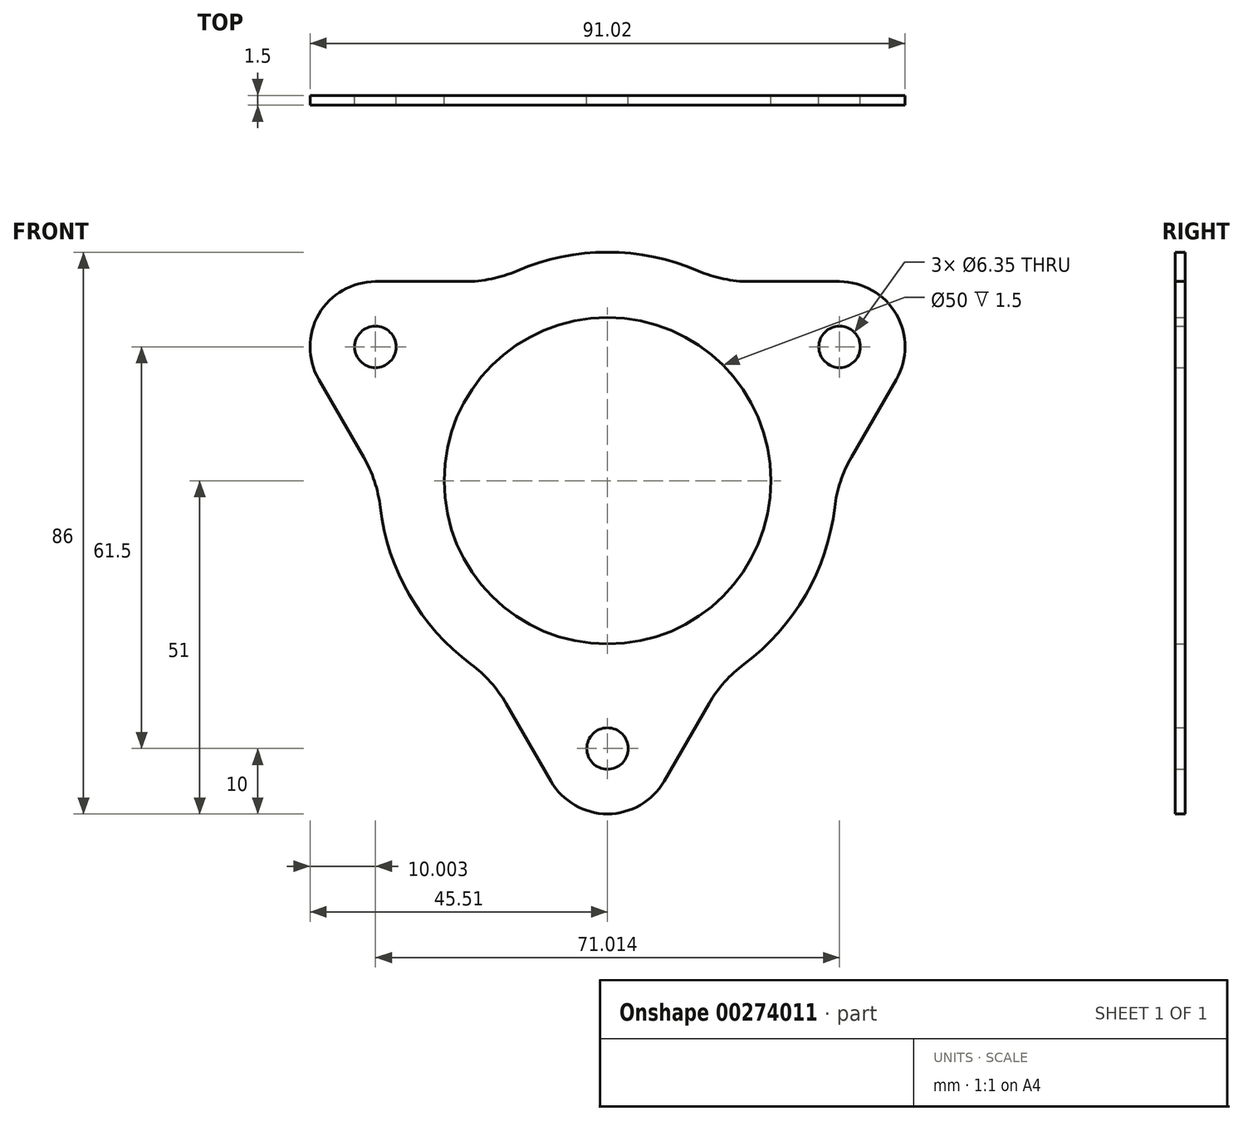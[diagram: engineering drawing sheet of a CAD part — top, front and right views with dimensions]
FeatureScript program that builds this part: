
annotation { "Feature Type Name" : "Feature", "Feature Type Description" : "" }
export const myFeature = defineFeature(function(context is Context, id is Id, definition is map)
    precondition{}
    {
        {
            var Q0;
            Q0=qCreatedBy(makeId("Front.planeOp"),FACE);
            var sketch = newSketch(context, id + "F0", { "sketchPlane" : qUnion([Q0])});
            skCircle(sketch, "E0", {"center": v(0, 0) * mm, "radius": 25 * mm});
            skCircle(sketch, "E1", {"center": v(0, 0) * mm, "radius": 41 * mm, "construction": true});
            skLineSegment(sketch, "E2", {"start": v(0, 0) * mm, "end": v(35.5, 20.5) * mm, "construction": true});
            skLineSegment(sketch, "E3", {"start": v(0, 0) * mm, "end": v(0, -41) * mm, "construction": true});
            skLineSegment(sketch, "E4", {"start": v(0, 0) * mm, "end": v(-35.5, 20.5) * mm, "construction": true});
            skCircle(sketch, "E5", {"center": v(-35.5, 20.5) * mm, "radius": 3.17 * mm});
            skCircle(sketch, "E6", {"center": v(35.5, 20.5) * mm, "radius": 3.17 * mm});
            skCircle(sketch, "E7", {"center": v(0, -41) * mm, "radius": 3.17 * mm});
            skArc(sketch, "E8", {"start": v(-8.66, -46) * mm, "mid": v(0, -51) * mm, "end": v(8.66, -46) * mm});
            skArc(sketch, "E9", {"start": v(-35.5, 30.5) * mm, "mid": v(-44.17, 25.5) * mm, "end": v(-44.17, 15.5) * mm});
            skArc(sketch, "E10", {"start": v(44.17, 15.5) * mm, "mid": v(44.17, 25.5) * mm, "end": v(35.5, 30.5) * mm});
            skLineSegment(sketch, "E11", {"start": v(-35.5, 30.5) * mm, "end": v(-17.17, 30.5) * mm});
            skLineSegment(sketch, "E12", {"start": v(-44.17, 15.5) * mm, "end": v(-35, -0.38) * mm});
            skLineSegment(sketch, "E13", {"start": v(8.66, -46) * mm, "end": v(17.83, -30.12) * mm});
            skArc(sketch, "E14", {"start": v(-35, -0.38) * mm, "mid": v(-30.31, -17.5) * mm, "end": v(-17.83, -30.12) * mm});
            skLineSegment(sketch, "E15.trimOffspring", {"start": v(17.17, 30.5) * mm, "end": v(35.5, 30.5) * mm});
            skLineSegment(sketch, "E16.trimOffspring", {"start": v(-17.83, -30.12) * mm, "end": v(-8.66, -46) * mm});
            skArc(sketch, "E17.trimOffspring", {"start": v(17.83, -30.12) * mm, "mid": v(30.31, -17.5) * mm, "end": v(35, -0.38) * mm});
            skLineSegment(sketch, "E18.trimOffspring", {"start": v(35, -0.38) * mm, "end": v(44.17, 15.5) * mm});
            skArc(sketch, "E19.trimOffspring", {"start": v(17.17, 30.5) * mm, "mid": v(0, 35) * mm, "end": v(-17.17, 30.5) * mm});
            skSolve(sketch);
        }
        {
            var Q0;
            Q0=qSketchRegion(id+"F0",true);
            extrude(context, id + "F1", {"entities" : qUnion([Q0]), "depth" : 1.5 * mm});
        }
        {
            var Q0;
            Q0=makeQuery(id+"F1.opExtrude","SWEPT_EDGE",EDGE,{"disambiguationData":[OSD([sQuery(id+"F0.wireOp",EDGE,"E17.trimOffspring"),sQuery(id+"F0.wireOp",EDGE,"E18.trimOffspring")])]});
            var Q1;
            Q1=makeQuery(id+"F1.opExtrude","SWEPT_EDGE",EDGE,{"disambiguationData":[OSD([sQuery(id+"F0.wireOp",EDGE,"E15.trimOffspring"),sQuery(id+"F0.wireOp",EDGE,"E19.trimOffspring")])]});
            var Q2;
            Q2=makeQuery(id+"F1.opExtrude","SWEPT_EDGE",EDGE,{"disambiguationData":[OSD([sQuery(id+"F0.wireOp",EDGE,"E11"),sQuery(id+"F0.wireOp",EDGE,"E19.trimOffspring")])]});
            var Q3;
            Q3=makeQuery(id+"F1.opExtrude","SWEPT_EDGE",EDGE,{"disambiguationData":[OSD([sQuery(id+"F0.wireOp",EDGE,"E12"),sQuery(id+"F0.wireOp",EDGE,"E14")])]});
            var Q4;
            Q4=makeQuery(id+"F1.opExtrude","SWEPT_EDGE",EDGE,{"disambiguationData":[OSD([sQuery(id+"F0.wireOp",EDGE,"E14"),sQuery(id+"F0.wireOp",EDGE,"E16.trimOffspring")])]});
            var Q5;
            Q5=makeQuery(id+"F1.opExtrude","SWEPT_EDGE",EDGE,{"disambiguationData":[OSD([sQuery(id+"F0.wireOp",EDGE,"E13"),sQuery(id+"F0.wireOp",EDGE,"E17.trimOffspring")])]});
            fillet(context, id + "F2", {"entities" : qUnion([Q0, Q1, Q2, Q3, Q4, Q5]), "radius" : 20 * mm, "tangentPropagation" : true, "allowEdgeOverflow" : false});
        }
    });
